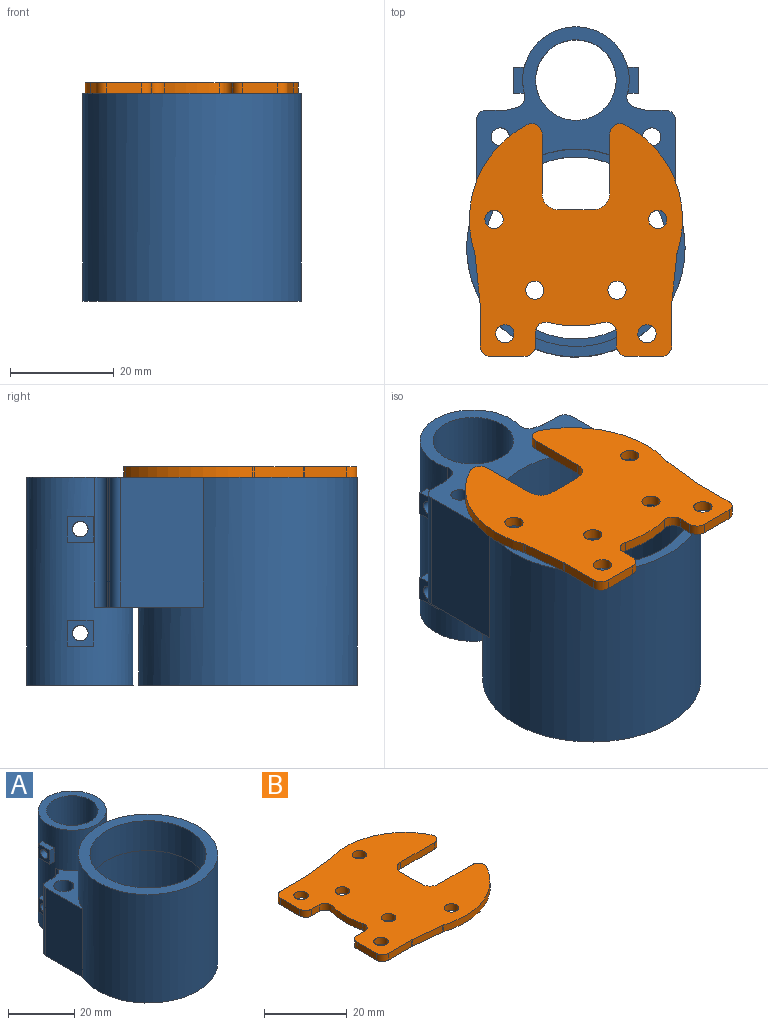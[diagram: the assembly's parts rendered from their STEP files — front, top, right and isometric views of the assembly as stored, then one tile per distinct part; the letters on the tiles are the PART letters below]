
ASSEMBLY  parts=2 mates=1
PART A: 52 faces, bbox 42x63.5x40 mm
  f0: cylinder r=17.5mm len=35mm, axis (0,0,-1), area 1209.5mm2, adj f2,f5
  f1: cylinder r=21mm len=42mm, axis (0,0,-1), area 4071.8mm2, adj f2,f3,f12,f13,f15
  f2: plane 42x42mm, normal (0,0,1), area 423.3mm2, adj f0,f1
  f3: plane 63.5x42mm, normal (0,0,-1), area 669mm2, adj f1,f4,f6,f7,f9,f10,f11,f12
  f4: cylinder r=19mm len=38mm, axis (0,0,-1), area 3462mm2, adj f3,f5
  f5: plane 38x38mm, normal (0,0,-1), area 172mm2, adj f0,f4
  f6: cylinder r=10.25mm len=40mm, axis (0,0,-1), area 1809.6mm2, adj f3,f8,f15,f16,f17,f19,f20,f21
  f7: cylinder r=7.75mm len=40mm, axis (0,0,-1), area 1919.5mm2, adj f3,f8,f36,f37,f38,f39
  f8: plane 20.5x20.5mm, normal (0,0,1), area 141.4mm2, adj f6,f7
  f9: plane 25x1.59mm, normal (-0.28,0.96,0), area 41.4mm2, adj f3,f15,f46,f51
  f10: plane 25x1.59mm, normal (0.28,0.96,0), area 41.4mm2, adj f3,f15,f47,f48
  f11: plane 25x3.77mm, normal (0,1,0), area 94.2mm2, adj f3,f15,f48,f49
  f12: plane 25x15.89mm, normal (1,0,0), area 397.2mm2, adj f1,f3,f15,f49
  f13: plane 25x15.89mm, normal (-1,0,0), area 397.2mm2, adj f1,f3,f15,f50
  f14: plane 25x3.77mm, normal (0,1,0), area 94.2mm2, adj f3,f15,f50,f51
  f15: plane 38.31x20.89mm, normal (0,0,1), area 239mm2, adj f1,f6,f9,f10,f11,f12,f13,f14
  f16: plane 5x2.06mm, normal (0,0,1), area 9.3mm2, adj f6,f17,f18,f19
  f17: plane 5x2.06mm, normal (0,-1,0), area 10.3mm2, adj f6,f16,f18,f20
  f18: plane 5x5mm, normal (1,0,0), area 17.9mm2, adj f16,f17,f19,f20,f39
  f19: plane 5x2.06mm, normal (0,1,0), area 10.3mm2, adj f6,f16,f18,f20
  f20: plane 5x2.06mm, normal (0,0,-1), area 9.3mm2, adj f6,f17,f18,f19
  f21: plane 5x2.06mm, normal (0,0,1), area 9.3mm2, adj f6,f22,f23,f24
  f22: plane 5x2.06mm, normal (0,-1,0), area 10.3mm2, adj f6,f21,f23,f25
  f23: plane 5x5mm, normal (1,0,0), area 17.9mm2, adj f21,f22,f24,f25,f38
  f24: plane 5x2.06mm, normal (0,1,0), area 10.3mm2, adj f6,f21,f23,f25
  f25: plane 5x2.06mm, normal (0,0,-1), area 9.3mm2, adj f6,f22,f23,f24
  f26: plane 5x2.06mm, normal (0,0,-1), area 9.3mm2, adj f6,f27,f28,f29
  f27: plane 5x2.06mm, normal (0,-1,0), area 10.3mm2, adj f6,f26,f28,f30
  f28: plane 5x5mm, normal (-1,0,0), area 17.9mm2, adj f26,f27,f29,f30,f37
  f29: plane 5x2.06mm, normal (0,1,0), area 10.3mm2, adj f6,f26,f28,f30
  f30: plane 5x2.06mm, normal (0,0,1), area 9.3mm2, adj f6,f27,f28,f29
  f31: plane 5x2.06mm, normal (0,0,-1), area 9.3mm2, adj f6,f32,f33,f34
  f32: plane 5x2.06mm, normal (0,-1,0), area 10.3mm2, adj f6,f31,f33,f35
  f33: plane 5x5mm, normal (-1,0,0), area 17.9mm2, adj f31,f32,f34,f35,f36
  f34: plane 5x2.06mm, normal (0,1,0), area 10.3mm2, adj f6,f31,f33,f35
  f35: plane 5x2.06mm, normal (0,0,1), area 9.3mm2, adj f6,f32,f33,f34
  f36: cylinder r=1.5mm len=4.4mm, axis (1,0,0), area 40.7mm2, adj f7,f33
  f37: cylinder r=1.5mm len=4.4mm, axis (1,0,0), area 40.7mm2, adj f7,f28
  f38: cylinder r=1.5mm len=4.4mm, axis (1,0,0), area 40.7mm2, adj f7,f23
  f39: cylinder r=1.5mm len=4.4mm, axis (1,0,0), area 40.7mm2, adj f7,f18
  f40: cylinder r=3mm len=15mm, axis (0,0,1), area 282.7mm2, adj f15,f41
  f41: plane 6x6mm, normal (0,0,1), area 18.7mm2, adj f40,f42
  f42: cylinder r=1.75mm len=10mm, axis (0,0,1), area 110mm2, adj f3,f41
  f43: cylinder r=3mm len=15mm, axis (0,0,1), area 282.7mm2, adj f15,f44
  f44: plane 6x6mm, normal (0,0,1), area 18.7mm2, adj f43,f45
  f45: cylinder r=1.75mm len=10mm, axis (0,0,1), area 110mm2, adj f3,f44
  f46: cylinder r=2mm len=25mm, axis (0,0,-1), area 77.9mm2, adj f3,f6,f9,f15
  f47: cylinder r=2mm len=25mm, axis (0,0,-1), area 77.9mm2, adj f3,f6,f10,f15
  f48: cylinder r=2mm len=25mm, axis (0,0,1), area 14.2mm2, adj f3,f10,f11,f15
  f49: cylinder r=2mm len=25mm, axis (0,0,-1), area 78.5mm2, adj f3,f11,f12,f15
  f50: cylinder r=2mm len=25mm, axis (0,0,-1), area 78.5mm2, adj f3,f13,f14,f15
  f51: cylinder r=2mm len=25mm, axis (0,0,1), area 14.2mm2, adj f3,f9,f14,f15
PART B: 36 faces, bbox 44.8x41x2 mm
  f0: cylinder r=20.5mm len=24.53mm, axis (0,0,-1), area 57.7mm2, adj f6,f10,f11,f31
  f1: cylinder r=20.5mm len=10.56mm, axis (0,0,-1), area 21.4mm2, adj f10,f11,f25,f35
  f2: cylinder r=3mm len=3mm, axis (0,0,-1), area 9.4mm2, adj f3,f9,f10,f11
  f3: plane 11.53x2mm, normal (0,-1,0), area 23.1mm2, adj f2,f4,f10,f11
  f4: cylinder r=2mm len=2.92mm, axis (0,0,-1), area 8.2mm2, adj f3,f5,f10,f11
  f5: cylinder r=20.5mm len=24.53mm, axis (0,0,-1), area 57.7mm2, adj f4,f10,f11,f21
  f6: cylinder r=2mm len=2.92mm, axis (0,0,-1), area 8.2mm2, adj f0,f7,f10,f11
  f7: plane 11.53x2mm, normal (0,1,0), area 23.1mm2, adj f6,f8,f10,f11
  f8: cylinder r=3mm len=3mm, axis (0,0,-1), area 9.4mm2, adj f7,f9,f10,f11
  f9: plane 7x2mm, normal (1,0,0), area 14mm2, adj f2,f8,f10,f11
  f10: plane 44.76x41mm, normal (0,0,1), area 1268.5mm2, adj f0,f1,f2,f3,f4,f5,f6,f7
  f11: plane 44.76x41mm, normal (0,0,-1), area 1268.5mm2, adj f0,f1,f2,f3,f4,f5,f6,f7
  f12: cylinder r=1.75mm len=3.5mm, axis (0,0,1), area 22mm2, adj f10,f11
  f13: cylinder r=1.75mm len=3.5mm, axis (0,0,1), area 22mm2, adj f10,f11
  f14: cylinder r=1.75mm len=3.5mm, axis (0,0,1), area 22mm2, adj f10,f11
  f15: cylinder r=1.75mm len=3.5mm, axis (0,0,1), area 22mm2, adj f10,f11
  f16: plane 9.39x2mm, normal (-0.1,0.99,0), area 18.9mm2, adj f10,f11,f21,f22
  f17: plane 8x2mm, normal (0,1,0), area 16mm2, adj f10,f11,f22,f23
  f18: plane 6.63x2mm, normal (-1,0,0), area 13.3mm2, adj f10,f11,f23,f24
  f19: cylinder r=1.75mm len=3.5mm, axis (0,0,1), area 22mm2, adj f10,f11
  f20: plane 2.59x2mm, normal (0,-1,0), area 5.2mm2, adj f10,f11,f24,f25
  f21: cylinder r=2mm len=2mm, axis (0,0,-1), area 0.8mm2, adj f5,f10,f11,f16
  f22: cylinder r=2mm len=2mm, axis (0,0,-1), area 0.4mm2, adj f10,f11,f16,f17
  f23: cylinder r=2mm len=2mm, axis (0,0,1), area 6.3mm2, adj f10,f11,f17,f18
  f24: cylinder r=2mm len=2mm, axis (0,0,1), area 6.3mm2, adj f10,f11,f18,f20
  f25: cylinder r=2mm len=2.52mm, axis (0,0,-1), area 7.3mm2, adj f1,f10,f11,f20
  f26: plane 2.59x2mm, normal (0,1,0), area 5.2mm2, adj f10,f11,f34,f35
  f27: plane 6.63x2mm, normal (-1,0,0), area 13.3mm2, adj f10,f11,f33,f34
  f28: plane 8x2mm, normal (0,-1,0), area 16mm2, adj f10,f11,f32,f33
  f29: cylinder r=1.75mm len=3.5mm, axis (0,0,1), area 22mm2, adj f10,f11
  f30: plane 9.39x2mm, normal (-0.1,-0.99,0), area 18.9mm2, adj f10,f11,f31,f32
  f31: cylinder r=2mm len=2mm, axis (0,0,-1), area 0.8mm2, adj f0,f10,f11,f30
  f32: cylinder r=2mm len=2mm, axis (0,0,-1), area 0.4mm2, adj f10,f11,f28,f30
  f33: cylinder r=2mm len=2mm, axis (0,0,1), area 6.3mm2, adj f10,f11,f27,f28
  f34: cylinder r=2mm len=2mm, axis (0,0,1), area 6.3mm2, adj f10,f11,f26,f27
  f35: cylinder r=2mm len=2.52mm, axis (0,0,-1), area 7.3mm2, adj f1,f10,f11,f26
PLACE A rot(axis=(0,1,0),180deg) t=(0,-9.01,35)mm
PLACE B rot(axis=(0.71,0.71,0),180deg) t=(0,-35.83,37)mm
MATE fastened A.f0 <-> B.f10  axis (0,0,1) through (0,-41.26,35)mm
